FCSTD DOCUMENT  (FreeCAD 0.21R33694 (Git))
Label: intersecting
License: All rights reserved
LicenseURL: http://en.wikipedia.org/wiki/All_rights_reserved
objects: Sketcher::SketchObject×2, PartDesign::Body×1
note: 3 computed .brp shape members not serialized (recipe doc carries the construction recipe); baked Part::Feature solids carry a one-line shape summary decoded from their .brp

FEATURE [Sketcher::SketchObject] Sketch
  FullyConstrained = false
  MapMode = 5
  Support = -> [XY_Plane]
  sketch-geometry (4):
    g0: LineSegment StartX=-26.5511 StartY=29.1946 StartZ=0 EndX=45.0919 EndY=29.1946 EndZ=0
    g1: LineSegment StartX=45.0919 StartY=29.1946 StartZ=0 EndX=45.0919 EndY=-34.7221 EndZ=0
    g2: LineSegment StartX=45.0919 StartY=-34.7221 StartZ=0 EndX=-26.5511 EndY=-34.7221 EndZ=0
    g3: LineSegment StartX=-26.5511 StartY=-34.7221 StartZ=0 EndX=-26.5511 EndY=29.1946 EndZ=0
  constraints (8):
    c: Coincident(g0,g1)
    c: Coincident(g1,g2)
    c: Coincident(g2,g3)
    c: Coincident(g3,g0)
    c: Horizontal(g0)
    c: Horizontal(g2)
    c: Vertical(g1)
    c: Vertical(g3)
FEATURE [Sketcher::SketchObject] Sketch001
  FullyConstrained = false
  MapMode = 5
  Support = -> [XY_Plane]
  sketch-geometry (1):
    g0: LineSegment StartX=-112.944 StartY=-52.9841 StartZ=0 EndX=82.7606 EndY=-41.7675 EndZ=0
FEATURE [PartDesign::Body] Body
  Group = -> [Sketch,Sketch001]
  Origin = -> Origin
